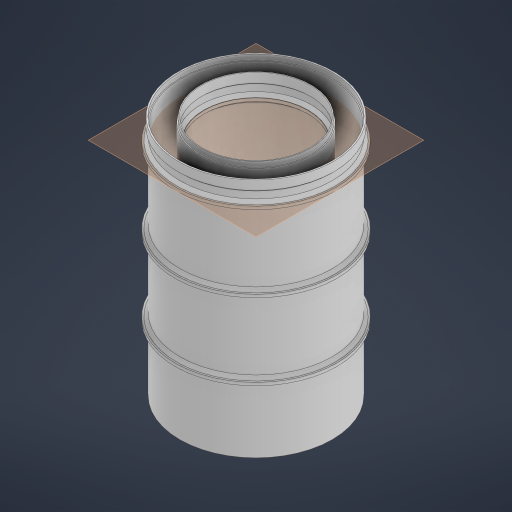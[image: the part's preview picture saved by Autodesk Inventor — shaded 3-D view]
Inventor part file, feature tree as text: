
AUTODESK INVENTOR PART (.ipt)
format: ipt  version: 2024 (Build 280153000, 153)  size: 407,040 bytes
history: native  units: mm
features: sketch x6, extrude x5, chamfer x3, shell x1, plane x1, pattern_linear x1
ambient origin geometry x8: Origin, YZ Plane, XZ Plane, XY Plane, X Axis, Y Axis, Z Axis, Center Point
bodies: Solid1 (feature_tree)
feature tree (17):
  extrude  "Extrusion1"  Depth=200.0mm
  shell  "Shell1"  Thickness=310.0mm
  sketch  "Sketch2"  dims[d4=1.0mm d5=360.0mm d7=360.0deg]
  extrude  "Extrusion2"  Depth=360.0mm TaperAngle=360.0deg
  extrude  "Extrusion3"  Depth=147.0mm
  extrude  "Extrusion4"  Depth=7.0mm TaperAngle=0.0deg
  chamfer  "Chamfer1"  Distance=7.0mm
  chamfer  "Chamfer2"  Distance=1.5mm Angle=45.0deg
  plane  "Work Plane1"
  extrude  "Extrusion5"  [1 undecoded]
  chamfer  "Chamfer3"  Distance=4.0mm
  pattern_linear  "Rectangular Pattern1"  Count1=3  [1 undecoded]
  sketch  "Sketch1"  dims[d0=145.0mm d1=200.0mm d2=310.0mm d3=0.0mm]
  sketch  "Sketch4"  dims[d9=320.0mm d10=0.0mm d11=147.0mm]
  sketch  "Sketch5"  dims[d12=198.0mm d13=14.0mm d14=0.0mm d15=7.0mm d16=0.0mm d17=1.5mm d18=2.0mm d19=45.0deg]
  sketch  "Sketch6"  dims[d20=2.0mm d21=2.0mm d22=45.0deg d23=-20.0mm d24=4.0mm d25=0.0mm]
  sketch  "Sketch7"  dims[d26=4.0mm d27=2.0mm d28=45.0deg d29=30.0mm d31=100.0mm]
note: 2 required parameter values undecoded (feature->parameter linkage not recoverable at this tier; creation-order binding heuristic only, values carry confidence <= 0.55)
